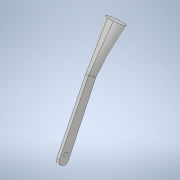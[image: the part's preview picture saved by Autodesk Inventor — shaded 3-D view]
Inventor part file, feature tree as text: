
AUTODESK INVENTOR PART (.ipt)
format: ipt  version: 2021 (Build 250183000, 183)  size: 187,392 bytes
history: native  units: mm
features: thicken_offset x4, sketch x2, extrude x1, fillet x1, plane x1, loft x1, other x1
ambient origin geometry x8: Origin, YZ Plane, XZ Plane, XY Plane, X Axis, Y Axis, Z Axis, Center Point
bodies: Solid1 (feature_tree)
feature tree (11):
  extrude  "Extrusion1"  Depth=50.0mm
  fillet  "Fillet1"  Radius=50.0mm
  thicken_offset  "Thicken1"
  thicken_offset  "Thicken2"
  thicken_offset  "Thicken3"
  plane  "Work Plane1"
  loft  "Loft1"
  thicken_offset  "Thicken4"
  sketch  "Sketch1"  dims[d2=0.0mm d5=50.0mm d7=50.0mm]
  sketch  "Sketch3"  dims[d9=50.0mm d12=0.0mm d13=90.0deg d14=0.0mm d15=90.0deg d17=40.0mm]
  other  "Edges1"
